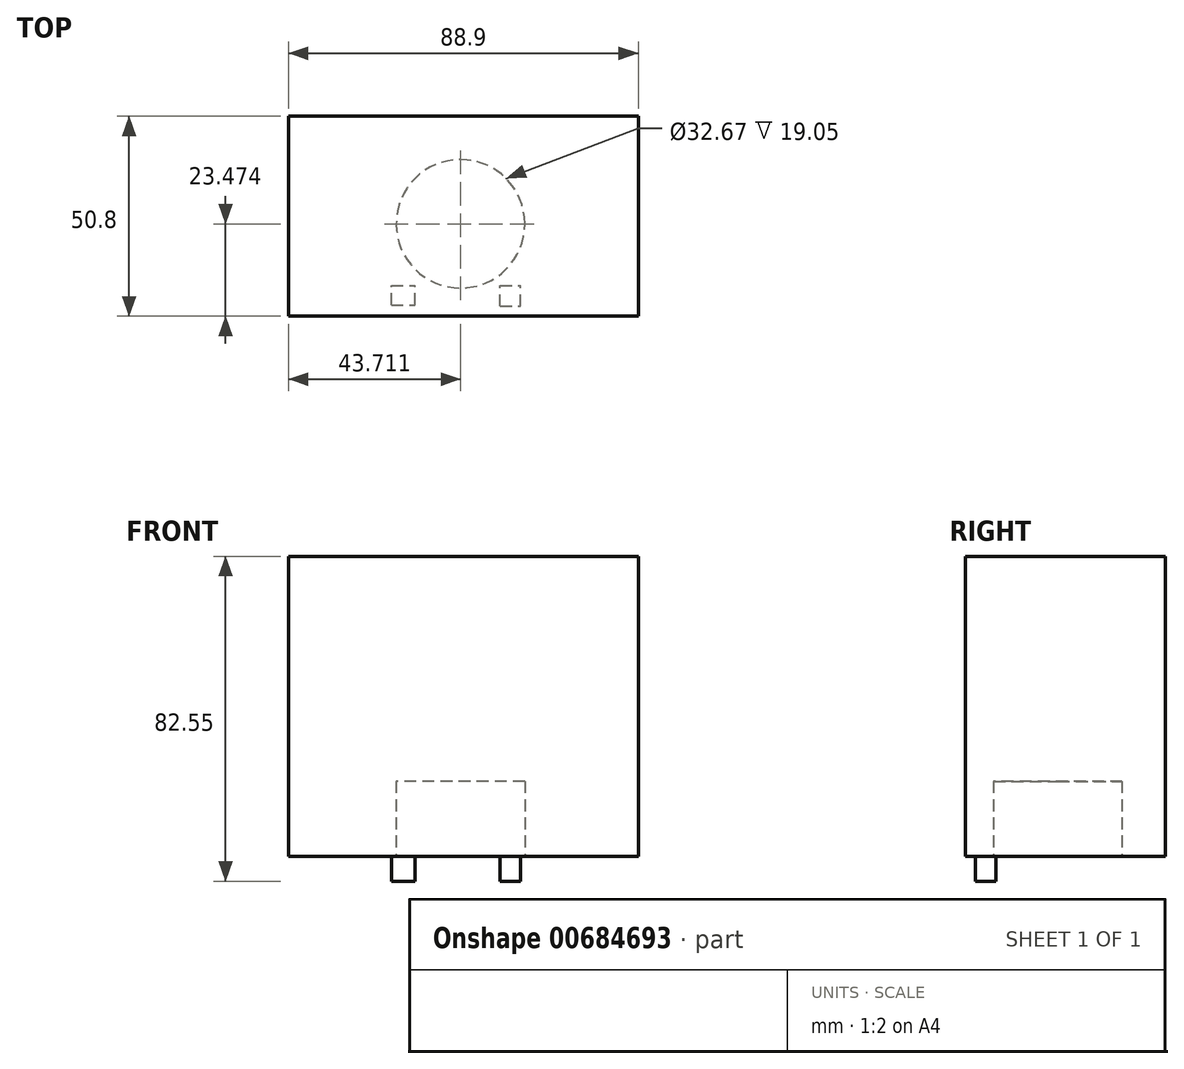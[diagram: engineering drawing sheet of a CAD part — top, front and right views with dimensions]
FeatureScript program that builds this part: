
annotation { "Feature Type Name" : "Feature", "Feature Type Description" : "" }
export const myFeature = defineFeature(function(context is Context, id is Id, definition is map)
    precondition{}
    {
        {
            var Q0;
            Q0=qCreatedBy(makeId("Top.planeOp"),FACE);
            var sketch = newSketch(context, id + "F0", { "sketchPlane" : qUnion([Q0])});
            skLineSegment(sketch, "E0.bottom", {"start": v(-48.46, 1.18) * mm, "end": v(40.44, 1.18) * mm});
            skLineSegment(sketch, "E0.top", {"start": v(-48.46, -49.62) * mm, "end": v(40.44, -49.62) * mm});
            skLineSegment(sketch, "E0.left", {"start": v(-48.46, 1.18) * mm, "end": v(-48.46, -49.62) * mm});
            skLineSegment(sketch, "E0.right", {"start": v(40.44, 1.18) * mm, "end": v(40.44, -49.62) * mm});
            skSolve(sketch);
        }
        {
            var Q0;
            Q0=qSketchRegion(id+"F0",true);
            extrude(context, id + "F1", {"entities" : qUnion([Q0]), "depth" : 76.2 * mm, "offsetDistance" : 25.4 * mm});
        }
        {
            var Q0;
            Q0=qCreatedBy(makeId("Top.planeOp"),FACE);
            var sketch = newSketch(context, id + "F2", { "sketchPlane" : qUnion([Q0])});
            skCircle(sketch, "E1", {"center": v(-4.75, -26.15) * mm, "radius": 16.34 * mm});
            skSolve(sketch);
        }
        {
            var Q0;
            Q0=qSketchRegion(id+"F2",true);
            extrude(context, id + "F3", {"entities" : qUnion([Q0]), "operationType" : NewBodyOperationType.REMOVE, "depth" : 19.05 * mm, "offsetDistance" : 25.4 * mm});
        }
        {
            var Q0;
            Q0=qCreatedBy(makeId("Top.planeOp"),FACE);
            var sketch = newSketch(context, id + "F4", { "sketchPlane" : qUnion([Q0])});
            skLineSegment(sketch, "E2.bottom", {"start": v(-24.32, -46.48) * mm, "end": v(-19.43, -46.48) * mm});
            skLineSegment(sketch, "E2.top", {"start": v(-24.32, -41.88) * mm, "end": v(-19.43, -41.88) * mm});
            skLineSegment(sketch, "E2.left", {"start": v(-24.32, -46.48) * mm, "end": v(-24.32, -41.88) * mm});
            skLineSegment(sketch, "E2.right", {"start": v(-19.43, -46.48) * mm, "end": v(-19.43, -41.88) * mm});
            skLineSegment(sketch, "E3.bottom", {"start": v(7.63, -46.2) * mm, "end": v(11.94, -46.2) * mm});
            skLineSegment(sketch, "E3.top", {"start": v(7.63, -42.16) * mm, "end": v(11.94, -42.16) * mm});
            skLineSegment(sketch, "E3.left", {"start": v(7.63, -46.2) * mm, "end": v(7.63, -42.16) * mm});
            skLineSegment(sketch, "E3.right", {"start": v(11.94, -46.2) * mm, "end": v(11.94, -42.16) * mm});
            skSolve(sketch);
        }
        {
            var Q0;
            Q0=qSketchRegion(id+"F4",true);
            extrude(context, id + "F5", {"entities" : qUnion([Q0]), "operationType" : NewBodyOperationType.ADD, "depth" : 12.7 * mm, "offsetDistance" : 25.4 * mm});
        }
        {
            var Q0;
            Q0=qCreatedBy(makeId("Top.planeOp"),FACE);
            var sketch = newSketch(context, id + "F6", { "sketchPlane" : qUnion([Q0])});
            skLineSegment(sketch, "E4.bottom", {"start": v(-22.3, -46.77) * mm, "end": v(-16.26, -46.77) * mm});
            skLineSegment(sketch, "E4.top", {"start": v(-22.3, -41.88) * mm, "end": v(-16.26, -41.88) * mm});
            skLineSegment(sketch, "E4.left", {"start": v(-22.3, -46.77) * mm, "end": v(-22.3, -41.88) * mm});
            skLineSegment(sketch, "E4.right", {"start": v(-16.26, -46.77) * mm, "end": v(-16.26, -41.88) * mm});
            skLineSegment(sketch, "E5.bottom", {"start": v(5.32, -47.06) * mm, "end": v(10.5, -47.06) * mm});
            skLineSegment(sketch, "E5.top", {"start": v(5.32, -41.88) * mm, "end": v(10.5, -41.88) * mm});
            skLineSegment(sketch, "E5.left", {"start": v(5.32, -47.06) * mm, "end": v(5.32, -41.88) * mm});
            skLineSegment(sketch, "E5.right", {"start": v(10.5, -47.06) * mm, "end": v(10.5, -41.88) * mm});
            skSolve(sketch);
        }
        {
            var Q0;
            Q0=qSketchRegion(id+"F6",true);
            extrude(context, id + "F7", {"entities" : qUnion([Q0]), "operationType" : NewBodyOperationType.ADD, "oppositeDirection" : true, "depth" : 6.35 * mm, "offsetDistance" : 25.4 * mm});
        }
    });
